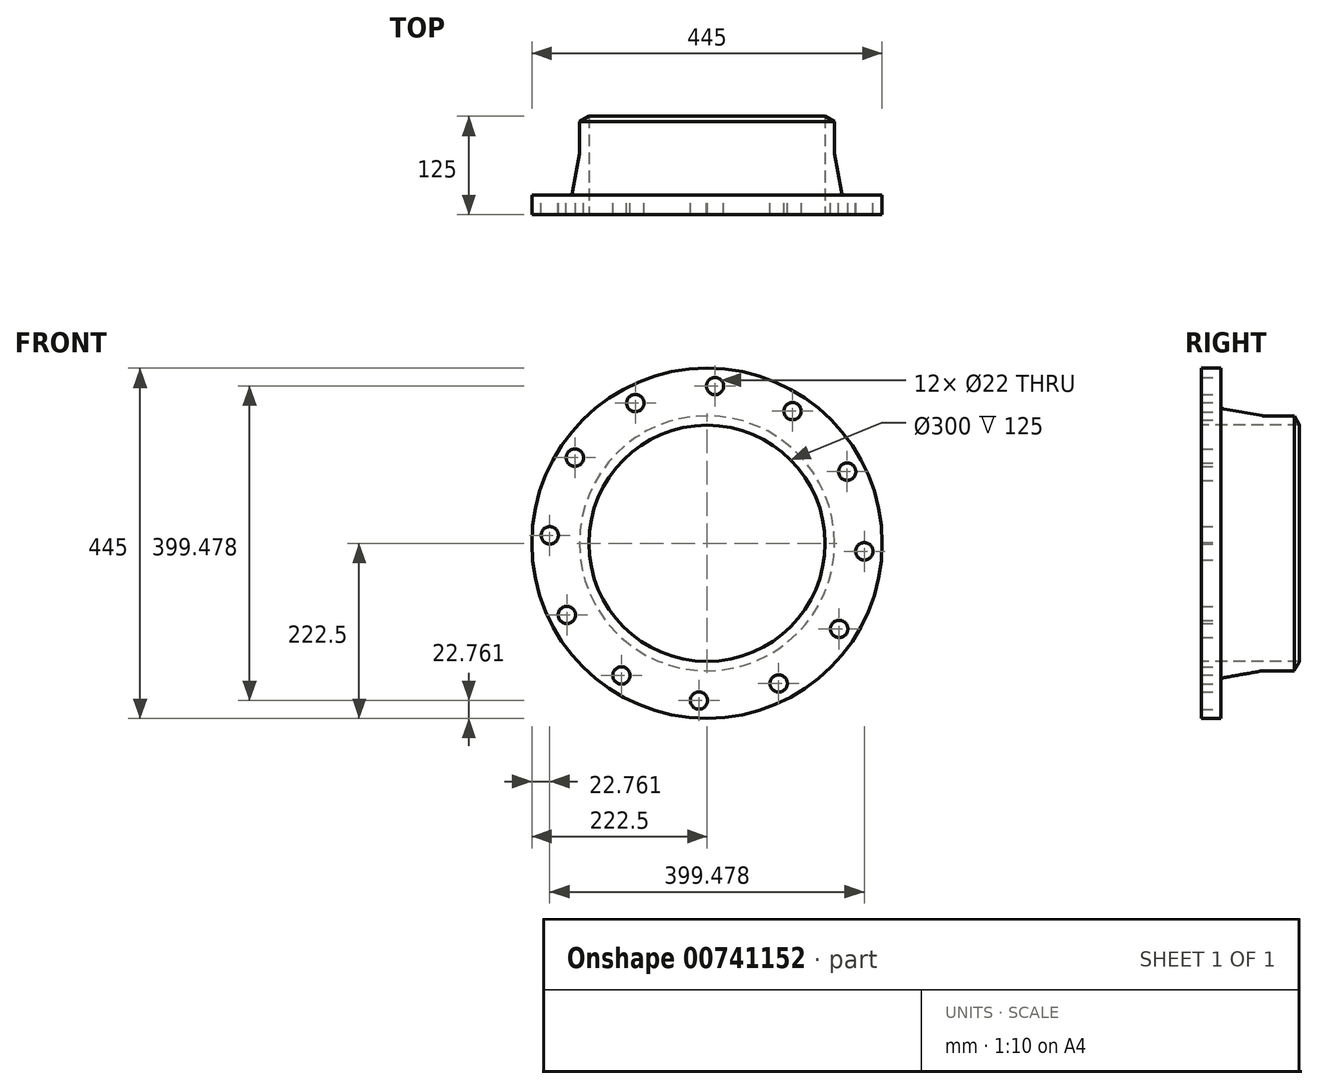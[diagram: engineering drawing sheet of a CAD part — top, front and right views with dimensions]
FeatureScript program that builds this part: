
annotation { "Feature Type Name" : "Feature", "Feature Type Description" : "" }
export const myFeature = defineFeature(function(context is Context, id is Id, definition is map)
    precondition{}
    {
        {
            var Q0;
            Q0=qCreatedBy(makeId("Top.planeOp"),FACE);
            var sketch = newSketch(context, id + "F0", { "sketchPlane" : qUnion([Q0])});
            skLineSegment(sketch, "E0", {"start": v(0, -499.79) * mm, "end": v(0, 756.89) * mm, "construction": true});
            skLineSegment(sketch, "E1", {"start": v(-150, 0) * mm, "end": v(-150, 125) * mm});
            skLineSegment(sketch, "E2", {"start": v(-150, 125) * mm, "end": v(-161.95, 118.1) * mm});
            skLineSegment(sketch, "E3", {"start": v(-161.95, 118.1) * mm, "end": v(-161.95, 78.1) * mm});
            skLineSegment(sketch, "E4", {"start": v(-161.95, 78.1) * mm, "end": v(-171.31, 25) * mm});
            skLineSegment(sketch, "E5", {"start": v(-171.31, 25) * mm, "end": v(-222.5, 25) * mm});
            skLineSegment(sketch, "E6", {"start": v(-222.5, 25) * mm, "end": v(-222.5, 0) * mm});
            skLineSegment(sketch, "E7", {"start": v(-222.5, 0) * mm, "end": v(-150, 0) * mm});
            skSolve(sketch);
        }
        {
            var Q0;
            Q0=makeQuery(id+"F0.imprint","IMPRINT",FACE,{"disambiguationData":[TD([[makeQuery(id+"F0.imprint","IMPRINT",EDGE,{"derivedFrom":sQuery(id+"F0.wireOp",EDGE,"E1")}),1.0]])]});
            var Q1;
            Q1=sQuery(id+"F0.wireOp",EDGE,"E0");
            revolve(context, id + "F1", {"surfaceOperationType" : NewSurfaceOperationType.NEW, "entities" : qUnion([Q0]), "axis" : qUnion([Q1]), "revolveType" : RevolveType.FULL});
        }
        {
            var Q0;
            Q0=makeQuery(id+"F1.opRevolve","SWEPT_EDGE",EDGE,{"disambiguationData":[OSD([sQuery(id+"F0.wireOp",EDGE,"E4"),sQuery(id+"F0.wireOp",EDGE,"E5")])]});
            var Q1;
            Q1=makeQuery(id+"F1.opRevolve","SWEPT_EDGE",EDGE,{"disambiguationData":[OSD([sQuery(id+"F0.wireOp",EDGE,"E3"),sQuery(id+"F0.wireOp",EDGE,"E4")])]});
            fillet(context, id + "F2", {"entities" : qUnion([Q0, Q1]), "radius" : 5 * mm, "tangentPropagation" : true, "allowEdgeOverflow" : false});
        }
        {
            var Q0;
            Q0=makeQuery(id+"F1.opRevolve","SWEPT_FACE",FACE,{"disambiguationData":[OSD([sQuery(id+"F0.wireOp",EDGE,"E5")])]});
            var sketch = newSketch(context, id + "F3", { "sketchPlane" : qUnion([Q0])});
            skCircle(sketch, "E8", {"center": v(0, 0) * mm, "radius": 200 * mm, "construction": true});
            skCircle(sketch, "E9", {"center": v(108.71, -167.87) * mm, "radius": 11 * mm});
            skCircle(sketch, "E10.1.0", {"center": v(178.09, -91.03) * mm, "radius": 11 * mm});
            skCircle(sketch, "E10.2.0", {"center": v(199.74, 10.21) * mm, "radius": 11 * mm});
            skCircle(sketch, "E10.3.0", {"center": v(167.87, 108.71) * mm, "radius": 11 * mm});
            skCircle(sketch, "E10.4.0", {"center": v(91.03, 178.09) * mm, "radius": 11 * mm});
            skCircle(sketch, "E10.5.0", {"center": v(-10.21, 199.74) * mm, "radius": 11 * mm});
            skCircle(sketch, "E10.6.0", {"center": v(-108.71, 167.87) * mm, "radius": 11 * mm});
            skCircle(sketch, "E10.7.0", {"center": v(-178.09, 91.03) * mm, "radius": 11 * mm});
            skCircle(sketch, "E10.8.0", {"center": v(-199.74, -10.21) * mm, "radius": 11 * mm});
            skCircle(sketch, "E10.9.0", {"center": v(-167.87, -108.71) * mm, "radius": 11 * mm});
            skCircle(sketch, "E10.10.0", {"center": v(-91.03, -178.09) * mm, "radius": 11 * mm});
            skCircle(sketch, "E10.11.0", {"center": v(10.21, -199.74) * mm, "radius": 11 * mm});
            skSolve(sketch);
        }
        {
            var Q0;
            Q0 = qSketchRegion(id + "F3", true);
            extrude(context, id + "F4", {"entities" : qUnion([Q0]), "operationType" : NewBodyOperationType.REMOVE, "oppositeDirection" : true, "depth" : 30 * mm, "offsetDistance" : 25 * mm});
        }
    });
